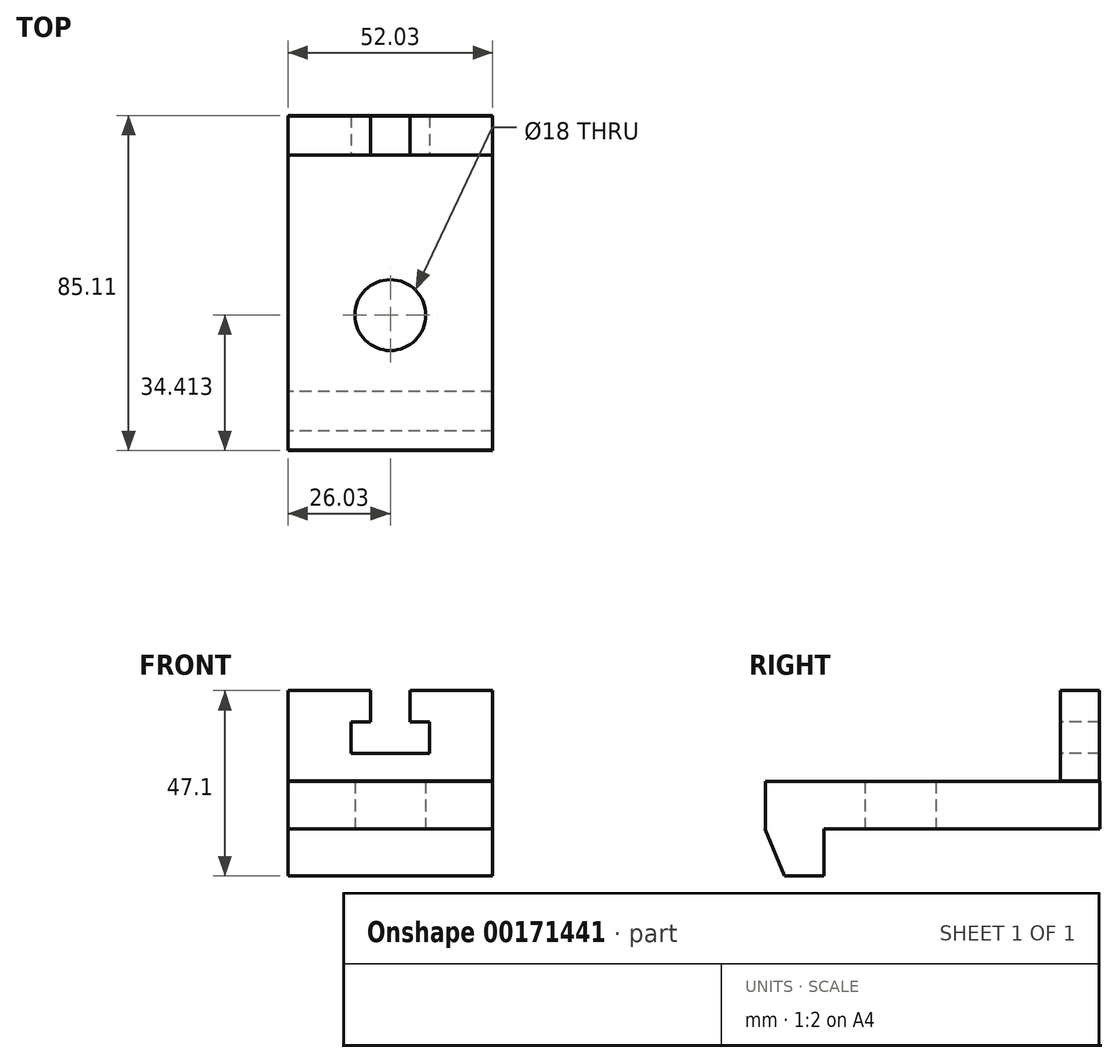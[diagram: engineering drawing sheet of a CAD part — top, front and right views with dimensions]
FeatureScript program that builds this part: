
annotation { "Feature Type Name" : "Feature", "Feature Type Description" : "" }
export const myFeature = defineFeature(function(context is Context, id is Id, definition is map)
    precondition{}
    {
        {
            var Q0;
            Q0=qCreatedBy(makeId("Top.planeOp"),FACE);
            var sketch = newSketch(context, id + "F0", { "sketchPlane" : qUnion([Q0])});
            skLineSegment(sketch, "E0.bottom", {"start": v(-26, 42.5) * mm, "end": v(26, 42.5) * mm});
            skLineSegment(sketch, "E0.top", {"start": v(-26, -42.5) * mm, "end": v(26, -42.5) * mm});
            skLineSegment(sketch, "E0.left", {"start": v(-26, 42.5) * mm, "end": v(-26, -42.5) * mm});
            skLineSegment(sketch, "E0.right", {"start": v(26, 42.5) * mm, "end": v(26, -42.5) * mm});
            skPoint(sketch, "E0.middle", {"position": v(0, 0) * mm});
            skSolve(sketch);
        }
        {
            var Q0;
            Q0=makeQuery(id+"F0.imprint","IMPRINT",FACE,{"disambiguationData":[TD([[makeQuery(id+"F0.imprint","IMPRINT",EDGE,{"derivedFrom":sQuery(id+"F0.wireOp",EDGE,"E0.bottom")}),-1.0]])]});
            extrude(context, id + "F1", {"entities" : qUnion([Q0]), "depth" : 12 * mm});
        }
        {
            var Q0;
            Q0=qCreatedBy(makeId("Top.planeOp"),FACE);
            var sketch = newSketch(context, id + "F2", { "sketchPlane" : qUnion([Q0])});
            skLineSegment(sketch, "E1", {"start": v(0, -43.2) * mm, "end": v(0, -8.2) * mm});
            skSolve(sketch);
        }
        {
            var Q0;
            Q0=sQuery(id+"F2.wireOp",VERTEX,"E1.end");
            var Q1;
            Q1=makeQuery(id+"F1.opExtrude","SWEPT_BODY",BODY,{"disambiguationData":[OSD([sQuery(id+"F0.wireOp",EDGE,"E0.bottom"),sQuery(id+"F0.wireOp",EDGE,"E0.top"),sQuery(id+"F0.wireOp",EDGE,"E0.left"),sQuery(id+"F0.wireOp",EDGE,"E0.right")])]});
            hole(context, id + "F3", {"style" : HoleStyle.SIMPLE, "endStyle" : HoleEndStyle.THROUGH, "oppositeDirection" : true, "holeDiameter" : 18 * mm, "locations" : qUnion([Q0]), "scope" : qUnion([Q1]), "isTappedThrough" : true});
        }
        {
            var Q0;
            Q0=qCreatedBy(makeId("Right.planeOp"),FACE);
            var sketch = newSketch(context, id + "F4", { "sketchPlane" : qUnion([Q0])});
            skLineSegment(sketch, "E2", {"start": v(-27.6, 0) * mm, "end": v(-27.6, -12) * mm});
            skLineSegment(sketch, "E3", {"start": v(-27.6, -12) * mm, "end": v(-37.6, -12) * mm});
            skLineSegment(sketch, "E4", {"start": v(-37.6, -12) * mm, "end": v(-42.6, 0) * mm});
            skLineSegment(sketch, "E5", {"start": v(-42.6, 0) * mm, "end": v(-27.6, 0) * mm});
            skSolve(sketch);
        }
        {
            var Q0;
            Q0 = qSketchRegion(id + "F4", true);
            extrude(context, id + "F5", {"entities" : qUnion([Q0]), "operationType" : NewBodyOperationType.ADD, "endBound" : BoundingType.SYMMETRIC, "depth" : 52 * mm});
        }
        {
            var Q0;
            Q0=qCreatedBy(makeId("Front.planeOp"),FACE);
            var sketch = newSketch(context, id + "F6", { "sketchPlane" : qUnion([Q0])});
            skLineSegment(sketch, "E6", {"start": v(-26.03, 12.1) * mm, "end": v(-26.03, 35.1) * mm});
            skLineSegment(sketch, "E7", {"start": v(-26.03, 35.1) * mm, "end": v(-5.03, 35.1) * mm});
            skLineSegment(sketch, "E8", {"start": v(-5.03, 35.1) * mm, "end": v(-5.03, 27.1) * mm});
            skLineSegment(sketch, "E9", {"start": v(-5.03, 27.1) * mm, "end": v(-10.03, 27.1) * mm});
            skLineSegment(sketch, "E10", {"start": v(-10.03, 27.1) * mm, "end": v(-10.03, 19.1) * mm});
            skLineSegment(sketch, "E11", {"start": v(-10.03, 19.1) * mm, "end": v(9.97, 19.1) * mm});
            skLineSegment(sketch, "E12", {"start": v(9.97, 19.1) * mm, "end": v(9.97, 27.1) * mm});
            skLineSegment(sketch, "E13", {"start": v(9.97, 27.1) * mm, "end": v(4.97, 27.1) * mm});
            skLineSegment(sketch, "E14", {"start": v(4.97, 27.1) * mm, "end": v(4.97, 35.1) * mm});
            skLineSegment(sketch, "E15", {"start": v(4.97, 35.1) * mm, "end": v(25.97, 35.1) * mm});
            skLineSegment(sketch, "E16", {"start": v(25.97, 35.1) * mm, "end": v(25.97, 12.1) * mm});
            skLineSegment(sketch, "E17", {"start": v(25.97, 12.1) * mm, "end": v(-26.03, 12.1) * mm});
            skSolve(sketch);
        }
        {
            var Q0;
            Q0=makeQuery(id+"F6.imprint","IMPRINT",FACE,{"disambiguationData":[TD([[makeQuery(id+"F6.imprint","IMPRINT",EDGE,{"derivedFrom":sQuery(id+"F6.wireOp",EDGE,"E6")}),-1.0]])]});
            extrude(context, id + "F7", {"entities" : qUnion([Q0]), "oppositeDirection" : true, "depth" : 42.4 * mm, "hasSecondDirection" : true, "secondDirectionOppositeDirection" : true, "secondDirectionDepth" : 32.4 * mm});
        }
    });
